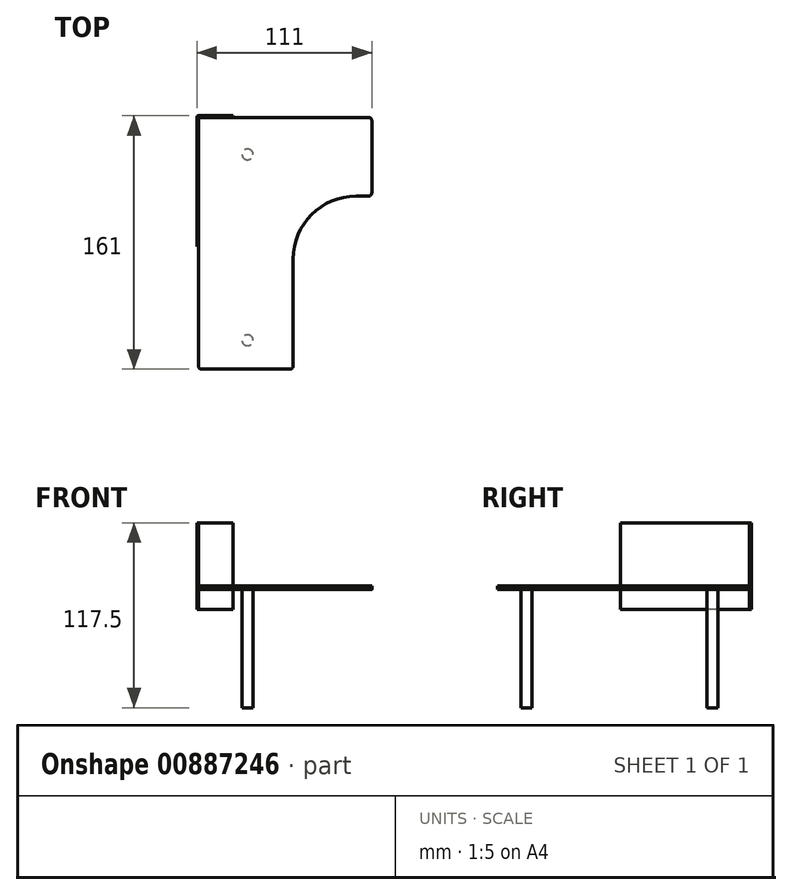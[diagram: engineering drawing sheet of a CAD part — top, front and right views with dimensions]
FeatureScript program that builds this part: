
annotation { "Feature Type Name" : "Feature", "Feature Type Description" : "" }
export const myFeature = defineFeature(function(context is Context, id is Id, definition is map)
    precondition{}
    {
        {
            var Q0;
            Q0=qCreatedBy(makeId("Top.planeOp"),FACE);
            var sketch = newSketch(context, id + "F0", { "sketchPlane" : qUnion([Q0])});
            skLineSegment(sketch, "E0", {"start": v(-2, 0) * mm, "end": v(-108, 0) * mm});
            skLineSegment(sketch, "E1", {"start": v(-110, -2) * mm, "end": v(-110, -158) * mm});
            skLineSegment(sketch, "E2", {"start": v(-108, -160) * mm, "end": v(-52, -160) * mm});
            skLineSegment(sketch, "E3", {"start": v(0, -2) * mm, "end": v(0, -48) * mm});
            skLineSegment(sketch, "E4", {"start": v(-2, -50) * mm, "end": v(-10, -50) * mm});
            skLineSegment(sketch, "E5", {"start": v(-50, -90) * mm, "end": v(-50, -158) * mm});
            skPoint(sketch, "E6.visualSharp", {"position": v(-50, -50) * mm});
            skArc(sketch, "E6.filletArc", {"start": v(-10, -50) * mm, "mid": v(-38.28, -61.72) * mm, "end": v(-50, -90) * mm});
            skPoint(sketch, "E7.visualSharp", {"position": v(-110, 0) * mm});
            skArc(sketch, "E7.filletArc", {"start": v(-108, 0) * mm, "mid": v(-109.41, -0.59) * mm, "end": v(-110, -2) * mm});
            skPoint(sketch, "E8.visualSharp", {"position": v(0, 0) * mm});
            skArc(sketch, "E8.filletArc", {"start": v(0, -2) * mm, "mid": v(-0.59, -0.59) * mm, "end": v(-2, 0) * mm});
            skPoint(sketch, "E9.visualSharp", {"position": v(-50, -160) * mm});
            skArc(sketch, "E9.filletArc", {"start": v(-52, -160) * mm, "mid": v(-50.59, -159.41) * mm, "end": v(-50, -158) * mm});
            skPoint(sketch, "E10.visualSharp", {"position": v(-110, -160) * mm});
            skArc(sketch, "E10.filletArc", {"start": v(-110, -158) * mm, "mid": v(-109.41, -159.41) * mm, "end": v(-108, -160) * mm});
            skPoint(sketch, "E11.visualSharp", {"position": v(0, -50) * mm});
            skArc(sketch, "E11.filletArc", {"start": v(-2, -50) * mm, "mid": v(-0.59, -49.41) * mm, "end": v(0, -48) * mm});
            skSolve(sketch);
        }
        {
            var Q0;
            Q0=makeQuery(id+"F0.imprint","IMPRINT",FACE,{"disambiguationData":[TD([[makeQuery(id+"F0.imprint","IMPRINT",EDGE,{"derivedFrom":sQuery(id+"F0.wireOp",EDGE,"E0")}),1.0]])]});
            extrude(context, id + "F1", {"entities" : qUnion([Q0]), "depth" : 2.5 * mm, "offsetDistance" : 25 * mm});
        }
        {
            var Q0;
            Q0=makeQuery(id+"F1.opExtrude","CAP_FACE",FACE,{"disambiguationData":[OSD([sQuery(id+"F0.wireOp",EDGE,"E0"),sQuery(id+"F0.wireOp",EDGE,"E1"),sQuery(id+"F0.wireOp",EDGE,"E2"),sQuery(id+"F0.wireOp",EDGE,"E3"),sQuery(id+"F0.wireOp",EDGE,"E4"),sQuery(id+"F0.wireOp",EDGE,"E5"),sQuery(id+"F0.wireOp",EDGE,"E6.filletArc"),sQuery(id+"F0.wireOp",EDGE,"E7.filletArc"),sQuery(id+"F0.wireOp",EDGE,"E8.filletArc"),sQuery(id+"F0.wireOp",EDGE,"E9.filletArc"),sQuery(id+"F0.wireOp",EDGE,"E10.filletArc"),sQuery(id+"F0.wireOp",EDGE,"E11.filletArc")])],"isStart":true});
            var sketch = newSketch(context, id + "F2", { "sketchPlane" : qUnion([Q0])});
            skCircle(sketch, "E12", {"center": v(-78.84, 141.6) * mm, "radius": 3.5 * mm});
            skCircle(sketch, "E13", {"center": v(-78.84, 23.55) * mm, "radius": 3.5 * mm});
            skSolve(sketch);
        }
        {
            var Q0;
            Q0=makeQuery(id+"F2.imprint","IMPRINT",FACE,{"disambiguationData":[TD([[makeQuery(id+"F2.imprint","IMPRINT",EDGE,{"derivedFrom":sQuery(id+"F2.wireOp",EDGE,"E12")}),1.0]])]});
            var Q1;
            Q1=makeQuery(id+"F2.imprint","IMPRINT",FACE,{"disambiguationData":[TD([[makeQuery(id+"F2.imprint","IMPRINT",EDGE,{"derivedFrom":sQuery(id+"F2.wireOp",EDGE,"E13")}),1.0]])]});
            extrude(context, id + "F3", {"entities" : qUnion([Q0, Q1]), "operationType" : NewBodyOperationType.ADD, "depth" : 75 * mm, "offsetDistance" : 25 * mm});
        }
        {
            var Q0;
            Q0=makeQuery(id+"F3.opExtrude","CAP_FACE",FACE,{"disambiguationData":[OSD([sQuery(id+"F2.wireOp",EDGE,"E12")])],"isStart":false});
            var sketch = newSketch(context, id + "F4", { "sketchPlane" : qUnion([Q0])});
            skCircle(sketch, "E14.0.0", {"center": v(-78.84, 141.6) * mm, "radius": 3.5 * mm});
            skLineSegment(sketch, "E15", {"start": v(-56.53, 141.6) * mm, "end": v(-104.53, 141.6) * mm});
            skArc(sketch, "E16.0.startCap", {"start": v(-56.53, 145.6) * mm, "mid": v(-52.53, 141.6) * mm, "end": v(-56.53, 137.6) * mm});
            skArc(sketch, "E16.0.endCap", {"start": v(-104.53, 137.6) * mm, "mid": v(-108.53, 141.6) * mm, "end": v(-104.53, 145.6) * mm});
            skLineSegment(sketch, "E16.0.left", {"start": v(-56.53, 137.6) * mm, "end": v(-104.53, 137.6) * mm});
            skLineSegment(sketch, "E16.0.right", {"start": v(-56.53, 145.6) * mm, "end": v(-104.53, 145.6) * mm});
            skCircle(sketch, "E17.0", {"center": v(-78.84, 23.55) * mm, "radius": 3.5 * mm});
            skLineSegment(sketch, "E18", {"start": v(-104.53, 23.55) * mm, "end": v(-15.07, 23.55) * mm});
            skArc(sketch, "E19.0.startCap", {"start": v(-104.53, 19.55) * mm, "mid": v(-108.53, 23.55) * mm, "end": v(-104.53, 27.55) * mm});
            skArc(sketch, "E19.0.endCap", {"start": v(-15.07, 27.55) * mm, "mid": v(-11.07, 23.55) * mm, "end": v(-15.07, 19.55) * mm});
            skLineSegment(sketch, "E19.0.left", {"start": v(-104.53, 27.55) * mm, "end": v(-15.07, 27.55) * mm});
            skLineSegment(sketch, "E19.0.right", {"start": v(-104.53, 19.55) * mm, "end": v(-15.07, 19.55) * mm});
            skSolve(sketch);
        }
        {
            var Q0;
            Q0=makeQuery(id+"F4.imprint","IMPRINT",FACE,{"disambiguationData":[TD([[makeQuery(id+"F4.imprint","IMPRINT",EDGE,{"derivedFrom":sQuery(id+"F4.wireOp",EDGE,"E16.0.startCap")}),-1.0]])]});
            var Q1;
            Q1=makeQuery(id+"F4.imprint","IMPRINT",FACE,{"disambiguationData":[TD([[makeQuery(id+"F4.imprint","IMPRINT",EDGE,{"derivedFrom":sQuery(id+"F4.wireOp",EDGE,"E19.0.startCap")}),-1.0]])]});
            var Q2;
            {var subQ0=sQuery(id+"F4.wireOp",EDGE,"E18");var subQ1=sQuery(id+"F4.wireOp",EDGE,"E17.0");var subQ2=makeQuery(id+"F4.imprint","INTERSECT",VERTEX,{"disambiguationData":[OD(0.0)],"derivedFrom":[subQ1,subQ0]});Q2=makeQuery(id+"F4.imprint","IMPRINT",FACE,{"disambiguationData":[TD([[makeQuery(id+"F4.imprint","IMPRINT",EDGE,{"disambiguationData":[TD([[subQ2,1.0]])],"derivedFrom":subQ1}),1.0]])]});}
            extrude(context, id + "F5", {"entities" : qUnion([Q0, Q1, Q2]), "operationType" : NewBodyOperationType.ADD, "oppositeDirection" : true, "depth" : 2 * mm, "offsetDistance" : 25 * mm});
        }
        {
            var Q0;
            Q0=makeQuery(id+"F1.opExtrude","CAP_FACE",FACE,{"disambiguationData":[OSD([sQuery(id+"F0.wireOp",EDGE,"E0"),sQuery(id+"F0.wireOp",EDGE,"E1"),sQuery(id+"F0.wireOp",EDGE,"E2"),sQuery(id+"F0.wireOp",EDGE,"E3"),sQuery(id+"F0.wireOp",EDGE,"E4"),sQuery(id+"F0.wireOp",EDGE,"E5"),sQuery(id+"F0.wireOp",EDGE,"E6.filletArc"),sQuery(id+"F0.wireOp",EDGE,"E7.filletArc"),sQuery(id+"F0.wireOp",EDGE,"E8.filletArc"),sQuery(id+"F0.wireOp",EDGE,"E9.filletArc"),sQuery(id+"F0.wireOp",EDGE,"E10.filletArc"),sQuery(id+"F0.wireOp",EDGE,"E11.filletArc")])],"isStart":false});
            var sketch = newSketch(context, id + "F6", { "sketchPlane" : qUnion([Q0])});
            skLineSegment(sketch, "E20", {"start": v(-88, 0) * mm, "end": v(-88, 1) * mm});
            skLineSegment(sketch, "E21", {"start": v(-88, 1) * mm, "end": v(-111, 1) * mm});
            skLineSegment(sketch, "E22", {"start": v(-111, 1) * mm, "end": v(-111, -82) * mm});
            skLineSegment(sketch, "E23", {"start": v(-111, -82) * mm, "end": v(-110, -82) * mm});
            skLineSegment(sketch, "E24", {"start": v(-110, -82) * mm, "end": v(-110, 0) * mm});
            skLineSegment(sketch, "E25", {"start": v(-110, 0) * mm, "end": v(-88, 0) * mm});
            skSolve(sketch);
        }
        {
            var Q0;
            {var subQ1=sQuery(id+"F6.wireOp",EDGE,"E20");Q0=makeQuery(id+"F6.imprint","IMPRINT",FACE,{"disambiguationData":[TD([[makeQuery(id+"F6.imprint","IMPRINT",EDGE,{"derivedFrom":subQ1}),1.0]])]});}
            extrude(context, id + "F7", {"entities" : qUnion([Q0]), "operationType" : NewBodyOperationType.ADD, "depth" : 40 * mm, "offsetDistance" : 25 * mm, "hasSecondDirection" : true, "secondDirectionOppositeDirection" : true, "secondDirectionDepth" : 15 * mm});
        }
        {
            var Q0;
            Q0=makeQuery(id+"F7.opExtrude","SWEPT_EDGE",EDGE,{"disambiguationData":[OSD([sQuery(id+"F6.wireOp",EDGE,"E21"),sQuery(id+"F6.wireOp",EDGE,"E22")])]});
            fillet(context, id + "F8", {"entities" : qUnion([Q0]), "radius" : 0.8 * mm, "tangentPropagation" : true, "allowEdgeOverflow" : false});
        }
    });
